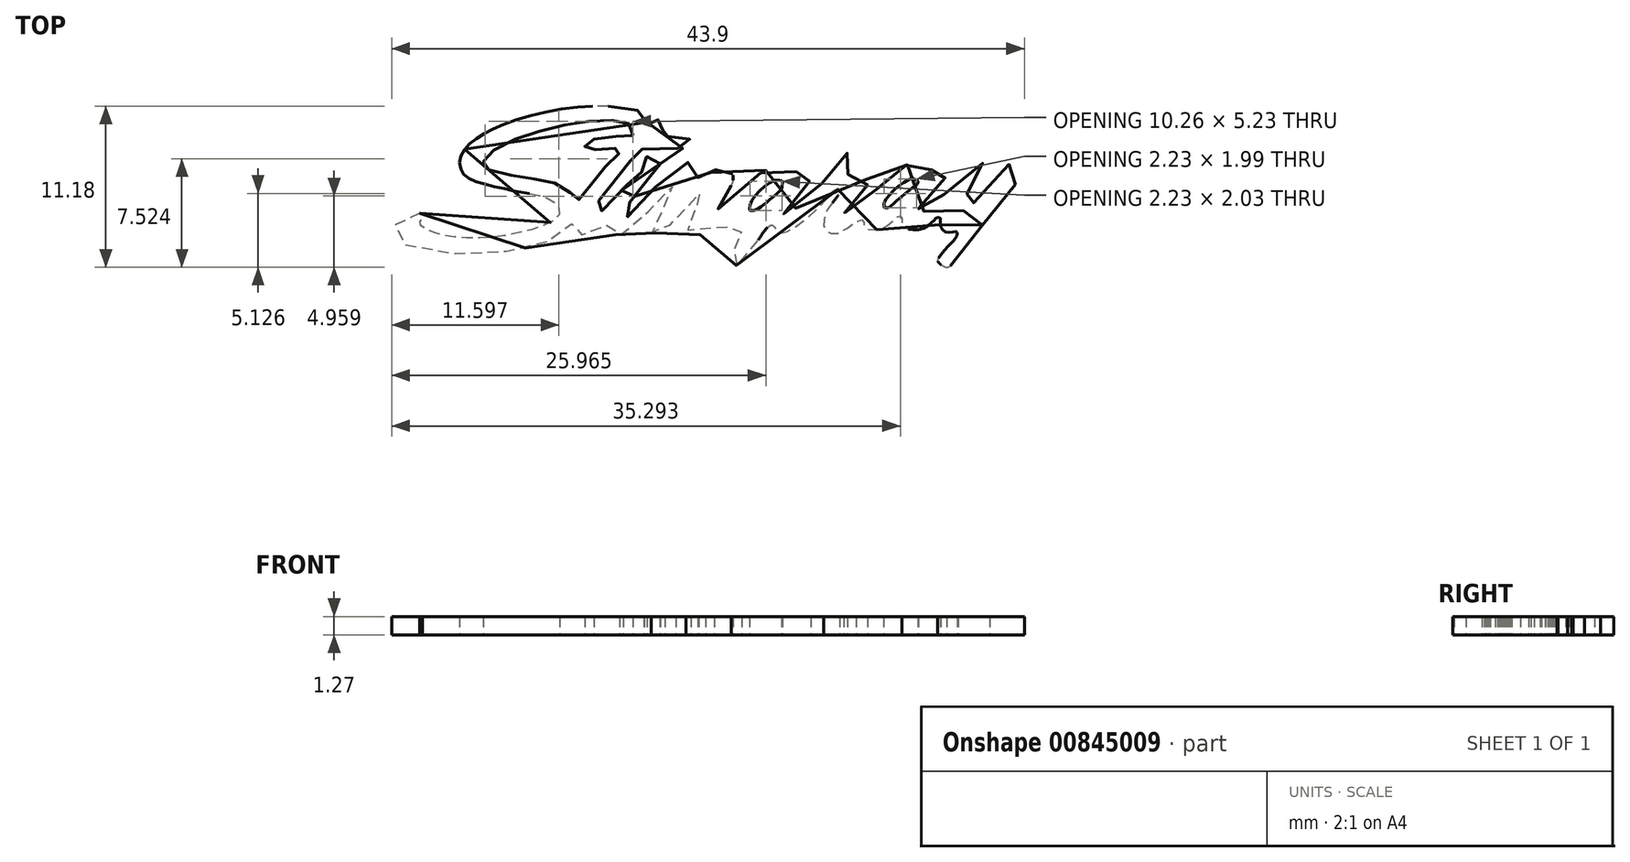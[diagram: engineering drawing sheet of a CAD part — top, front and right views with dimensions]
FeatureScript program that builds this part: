
annotation { "Feature Type Name" : "Feature", "Feature Type Description" : "" }
export const myFeature = defineFeature(function(context is Context, id is Id, definition is map)
    precondition{}
    {
        {
            var Q0;
            Q0=qCreatedBy(makeId("Top.planeOp"),FACE);
            var sketch = newSketch(context, id + "F0", { "sketchPlane" : qUnion([Q0])});
            skFitSpline(sketch, "E0", {"points": [v(-30.03, -0.78) * mm, v(-30.83, -0.97) * mm, v(-31.6, -1.4) * mm, v(-31.92, -1.96) * mm, v(-31.95, -2.29) * mm, v(-30.9, -3.01) * mm, v(-28.1, -3.54) * mm, v(-25.33, -3.57) * mm, v(-22.6, -3.15) * mm, v(-21.15, -2.7) * mm, v(-20.02, -2.07) * mm, v(-19.52, -1.53) * mm, v(-19.34, -1.42) * mm, v(-19.21, -1.52) * mm, v(-19.17, -1.74) * mm, v(-18.87, -2.2) * mm, v(-18.2, -2.27) * mm, v(-17.28, -1.62) * mm, v(-17.02, -1.64) * mm, v(-16.96, -1.88) * mm, v(-16.76, -2.18) * mm, v(-16.04, -2.25) * mm, v(-15.28, -1.73) * mm, v(-14, -0.47) * mm, v(-12.76, 0.91) * mm, v(-12.54, 1.08) * mm, v(-12.36, 1.1) * mm, v(-12.27, 0.97) * mm, v(-12.33, 0.68) * mm, v(-13.88, -1.27) * mm, v(-13.98, -1.68) * mm, v(-13.91, -2) * mm, v(-13.6, -2.16) * mm, v(-13.2, -2.15) * mm, v(-12.9, -1.89) * mm, v(-11.75, -0.53) * mm, v(-10.53, 0.65) * mm, v(-10.34, 0.73) * mm, v(-10.22, 0.68) * mm, v(-10.25, 0.5) * mm, v(-11.32, -0.84) * mm, v(-11.55, -1.55) * mm, v(-11.46, -1.91) * mm, v(-11.22, -2.15) * mm, v(-10.22, -2.18) * mm, v(-9.08, -1.34) * mm, v(-8.9, -1.28) * mm, v(-8.78, -1.39) * mm, v(-8.75, -1.66) * mm, v(-8.7, -1.77) * mm, v(-8.4, -1.96) * mm, v(-8.1, -1.95) * mm, v(-7.81, -2) * mm, v(-7.7, -2.15) * mm, v(-7.74, -2.44) * mm, v(-8.1, -3.11) * mm, v(-8.24, -3.35) * mm, v(-8.4, -3.64) * mm, v(-8.41, -4.1) * mm, v(-8.19, -4.36) * mm, v(-7.7, -4.39) * mm, v(-7.18, -3.7) * mm, v(-5.83, -1.67) * mm, v(-5.55, -1.6) * mm, v(-5.33, -1.89) * mm, v(-5.02, -2.1) * mm, v(-4.44, -2) * mm, v(-2.35, -0.35) * mm, v(-1.42, 0.71) * mm, v(-1.21, 0.86) * mm, v(-1, 0.9) * mm, v(-0.89, 0.75) * mm, v(-1.6, -0.3) * mm, v(-1.89, -0.84) * mm, v(-2, -1.33) * mm, v(-1.95, -1.82) * mm, v(-1.66, -2.1) * mm, v(-1.02, -2.17) * mm, v(0.4, -1.29) * mm, v(0.72, -1.25) * mm, v(0.78, -1.45) * mm, v(0.84, -1.73) * mm, v(1.13, -1.9) * mm, v(1.9, -1.87) * mm, v(2.5, -1.56) * mm, v(3.06, -1.08) * mm, v(3.22, -0.96) * mm, v(3.35, -0.97) * mm, v(3.43, -1.13) * mm, v(3.44, -1.49) * mm, v(3.62, -1.73) * mm, v(3.95, -1.89) * mm, v(4.76, -1.87) * mm, v(5.4, -1.48) * mm, v(5.67, -1.24) * mm, v(5.84, -1.09) * mm, v(6.02, -1.07) * mm, v(6.1, -1.2) * mm, v(6.08, -1.45) * mm, v(6.15, -1.78) * mm, v(6.4, -2.05) * mm, v(6.85, -2.09) * mm, v(7.17, -2.04) * mm, v(7.26, -2.14) * mm, v(7.18, -2.45) * mm, v(5.98, -3.82) * mm, v(5.96, -4.17) * mm, v(6.4, -4.49) * mm, v(6.76, -4.45) * mm, v(8.08, -3.04) * mm, v(8.87, -1.8) * mm, v(9.43, -1.03) * mm, v(10.52, 0.33) * mm, v(11.8, 1.86) * mm, v(11.89, 2.24) * mm, v(11.23, 2.69) * mm, v(10.87, 2.63) * mm, v(9.94, 1.45) * mm, v(8.64, 0.18) * mm, v(7.7, -0.57) * mm, v(7.41, -0.57) * mm, v(7.33, -0.41) * mm, v(8.18, 0.83) * mm, v(9.46, 2.06) * mm, v(9.5, 2.32) * mm, v(8.93, 2.73) * mm, v(8.29, 2.6) * mm, v(6.75, 0.93) * mm, v(5.5, -0.27) * mm, v(4.97, -0.64) * mm, v(4.6, -0.67) * mm, v(4.57, -0.43) * mm, v(4.7, -0.17) * mm, v(5.52, 0.9) * mm, v(6.44, 1.72) * mm, v(6.53, 2.1) * mm, v(6.27, 2.44) * mm, v(5.73, 2.47) * mm, v(5.54, 2.35) * mm, v(5.36, 2.22) * mm, v(5.17, 2.38) * mm, v(4.83, 2.57) * mm, v(4.24, 2.67) * mm, v(3.6, 2.5) * mm, v(2.74, 2.02) * mm, v(2.04, 1.36) * mm, v(1.51, 0.73) * mm, v(0.4, -0.16) * mm, v(-0.39, -0.71) * mm, v(-0.55, -0.73) * mm, v(-0.62, -0.63) * mm, v(0.07, 0.4) * mm, v(0.97, 1.13) * mm, v(1.04, 1.24) * mm, v(0.96, 1.51) * mm, v(0.84, 1.8) * mm, v(0.3, 1.9) * mm, v(-0.28, 1.9) * mm, v(-0.34, 2.02) * mm, v(0.2, 2.64) * mm, v(0.2, 3.14) * mm, v(-0.17, 3.43) * mm, v(-1.13, 2.77) * mm, v(-1.73, 1.82) * mm, v(-1.91, 1.54) * mm, v(-3.34, 0.13) * mm, v(-4.5, -0.78) * mm, v(-4.8, -0.8) * mm, v(-4.92, -0.68) * mm, v(-4.07, 0.53) * mm, v(-2.96, 1.51) * mm, v(-2.91, 1.87) * mm, v(-3.11, 2.06) * mm, v(-3.45, 2.31) * mm, v(-3.84, 2.23) * mm, v(-3.96, 2.1) * mm, v(-4.2, 2.1) * mm, v(-4.8, 2.47) * mm, v(-6.2, 2.12) * mm, v(-8, 0.61) * mm, v(-9.24, -0.43) * mm, v(-9.53, -0.5) * mm, v(-9.57, -0.3) * mm, v(-8.72, 0.82) * mm, v(-8.46, 1.1) * mm, v(-8.31, 1.37) * mm, v(-8.35, 2.02) * mm, v(-8.65, 2.28) * mm, v(-9.1, 2.36) * mm, v(-9.84, 2.07) * mm, v(-10.5, 1.62) * mm, v(-10.73, 1.66) * mm, v(-10.68, 2.32) * mm, v(-11.09, 2.7) * mm, v(-12.08, 2.57) * mm, v(-14.35, 0.29) * mm, v(-15.64, -1.03) * mm, v(-15.83, -1.11) * mm, v(-15.89, -0.8) * mm, v(-15.11, 0.44) * mm, v(-14.09, 1.63) * mm, v(-13.98, 2.04) * mm, v(-13.62, 2.22) * mm, v(-13.37, 2.59) * mm, v(-13.38, 3.04) * mm, v(-13.77, 3.32) * mm, v(-14.39, 3.07) * mm, v(-14.47, 2.7) * mm, v(-14.47, 2.3) * mm, v(-14.75, 2) * mm, v(-15.02, 1.88) * mm, v(-15.19, 1.72) * mm, v(-16.45, 0.39) * mm, v(-17.46, -0.64) * mm, v(-17.83, -0.86) * mm, v(-17.95, -0.72) * mm, v(-16.52, 1.64) * mm, v(-15, 3.28) * mm, v(-14.85, 3.46) * mm, v(-14.73, 3.6) * mm, v(-14.66, 3.65) * mm, v(-13.06, 3.83) * mm, v(-11.6, 3.74) * mm, v(-11.23, 3.97) * mm, v(-11.28, 4.34) * mm, v(-11.66, 4.58) * mm, v(-12.49, 4.59) * mm, v(-13.26, 4.59) * mm, v(-13.37, 4.66) * mm, v(-13.38, 4.8) * mm, v(-13.21, 4.99) * mm, v(-13.09, 5.13) * mm, v(-13.02, 5.34) * mm, v(-13.2, 5.66) * mm, v(-13.61, 5.68) * mm, v(-13.88, 5.51) * mm, v(-14.06, 5.38) * mm, v(-14.15, 5.33) * mm, v(-14.25, 5.45) * mm, v(-14.26, 5.7) * mm, v(-14.55, 6.12) * mm, v(-15.08, 6.44) * mm, v(-15.77, 6.57) * mm, v(-19.05, 6.6) * mm, v(-23.88, 5.54) * mm, v(-25.97, 4.5) * mm, v(-26.99, 3.58) * mm, v(-27.27, 2.66) * mm, v(-26.95, 1.88) * mm, v(-25.99, 1.39) * mm, v(-24.05, 0.9) * mm, v(-22.6, 0.61) * mm, v(-21.29, 0.32) * mm, v(-20.47, -0.23) * mm, v(-20.4, -0.95) * mm, v(-21.95, -1.8) * mm, v(-23.4, -2.17) * mm, v(-25.09, -2.45) * mm, v(-27.61, -2.42) * mm, v(-29.03, -2.11) * mm, v(-29.96, -1.64) * mm, v(-30.03, -1.36) * mm, v(-29.87, -1.19) * mm, v(-29.84, -1.02) * mm, v(-29.9, -0.84) * mm, v(-30.03, -0.78) * mm]});
            skFitSpline(sketch, "E1", {"points": [v(-6.15, -0.17) * mm, v(-5.85, 0.1) * mm, v(-5.48, 0.4) * mm, v(-5.1, 0.73) * mm, v(-4.89, 0.99) * mm, v(-4.88, 1.05) * mm, v(-4.88, 1.42) * mm, v(-4.92, 1.46) * mm, v(-5.02, 1.5) * mm, v(-5.4, 1.5) * mm, v(-6.32, 0.9) * mm, v(-6.98, 0.1) * mm, v(-7.16, -0.42) * mm, v(-7.14, -0.56) * mm, v(-6.92, -0.6) * mm, v(-6.46, -0.4) * mm, v(-6.15, -0.17) * mm]});
            skFitSpline(sketch, "E2", {"points": [v(3.08, 0.13) * mm, v(3.7, 0.62) * mm, v(4.2, 1.04) * mm, v(4.35, 1.14) * mm, v(4.5, 1.28) * mm, v(4.53, 1.44) * mm, v(4.37, 1.59) * mm, v(4.14, 1.64) * mm, v(3.88, 1.55) * mm, v(3.05, 0.99) * mm, v(2.4, 0.31) * mm, v(2.2, -0.05) * mm, v(2.2, -0.36) * mm, v(2.44, -0.4) * mm, v(2.68, -0.24) * mm, v(3.08, 0.13) * mm]});
            skFitSpline(sketch, "E3", {"points": [v(-15.26, 4.64) * mm, v(-15.33, 5.08) * mm, v(-15.53, 5.45) * mm, v(-15.88, 5.63) * mm, v(-17.25, 5.67) * mm, v(-18.6, 5.57) * mm, v(-20.2, 5.3) * mm, v(-22, 4.84) * mm, v(-23.56, 4.3) * mm, v(-24.91, 3.58) * mm, v(-25.5, 3.04) * mm, v(-25.63, 2.7) * mm, v(-25.55, 2.43) * mm, v(-25.3, 2.26) * mm, v(-24.07, 1.94) * mm, v(-22.56, 1.68) * mm, v(-21.32, 1.46) * mm, v(-20.31, 1.19) * mm, v(-19.58, 0.66) * mm, v(-19.3, 0.28) * mm, v(-19.06, 0.17) * mm, v(-18.8, 0.33) * mm, v(-17.99, 1.46) * mm, v(-17.07, 2.54) * mm, v(-16.27, 3.3) * mm, v(-16.2, 3.42) * mm, v(-16.18, 3.71) * mm, v(-16.33, 3.74) * mm, v(-17.04, 3.75) * mm, v(-18.16, 3.6) * mm, v(-18.55, 3.67) * mm, v(-18.57, 3.93) * mm, v(-18.4, 4.16) * mm, v(-17.94, 4.38) * mm, v(-16.66, 4.57) * mm, v(-15.43, 4.58) * mm, v(-15.26, 4.64) * mm]});
            skSolve(sketch);
        }
        {
            var Q0;
            Q0 = qSketchRegion(id + "F0", true);
            extrude(context, id + "F1", {"entities" : qUnion([Q0]), "depth" : 1.27 * mm, "offsetDistance" : 25.4 * mm});
        }
    });
